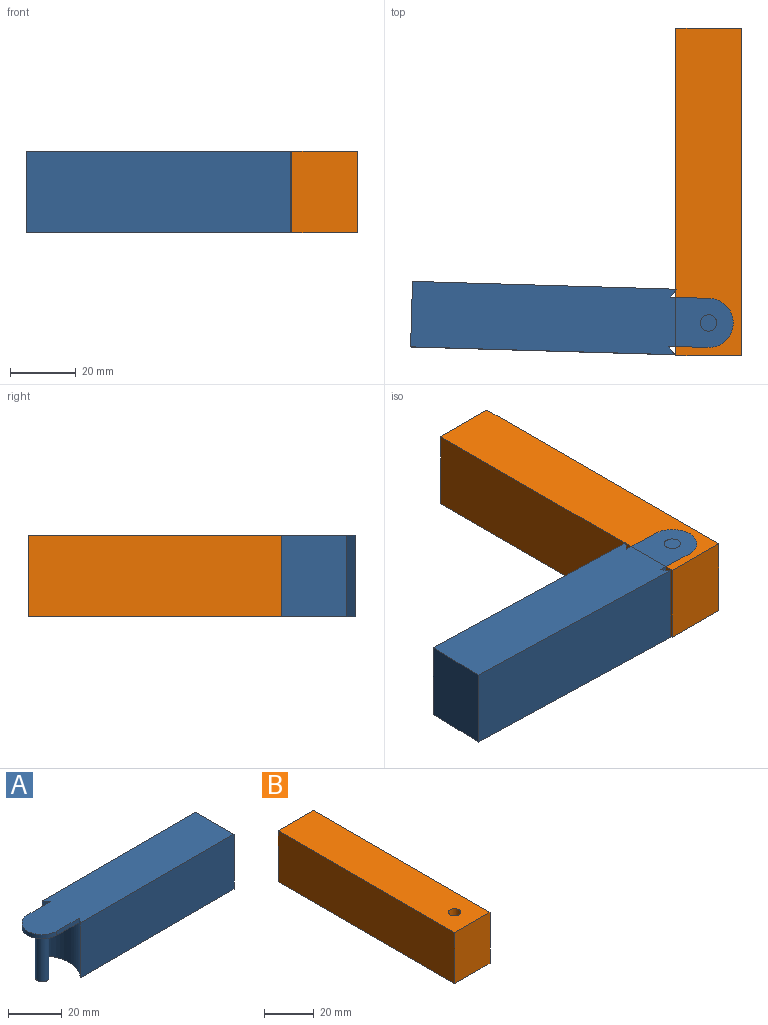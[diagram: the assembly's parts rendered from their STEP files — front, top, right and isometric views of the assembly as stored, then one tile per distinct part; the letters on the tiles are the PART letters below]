
ASSEMBLY  parts=2 mates=1
PART A: 12 faces, bbox 98.3x20x25 mm
  f0: cylinder r=14.14mm len=25mm, axis (0,0,-1), area 523.7mm2, adj f1,f3,f4,f5,f6,f8,f9
  f1: plane 80.76x25mm, normal (0,-1,0), area 2019.1mm2, adj f0,f2,f4,f5
  f2: plane 25x20mm, normal (1,0,0), area 500mm2, adj f1,f3,f4,f5
  f3: plane 80.76x25mm, normal (0,1,0), area 2019.1mm2, adj f0,f2,f4,f5
  f4: plane 98.26x20mm, normal (0,0,1), area 1848.3mm2, adj f0,f1,f2,f3,f7,f8,f9
  f5: plane 80.76x20mm, normal (0,0,-1), area 1558.2mm2, adj f0,f1,f2,f3
  f6: plane 21.64x15mm, normal (0,0,-1), area 270.4mm2, adj f0,f7,f8,f9,f10
  f7: cylinder r=7.5mm len=15mm, axis (0,0,1), area 47.1mm2, adj f4,f6,f8,f9
  f8: plane 11.99x2mm, normal (0,-1,0), area 24mm2, adj f0,f4,f6,f7
  f9: plane 11.99x2mm, normal (0,1,0), area 24mm2, adj f0,f4,f6,f7
  f10: cylinder r=2.5mm len=23mm, axis (0,0,1), area 361.3mm2, adj f6,f11
  f11: plane 5x5mm, normal (0,0,-1), area 19.6mm2, adj f10
PART B: 7 faces, bbox 20x100x25 mm
  f0: plane 100x25mm, normal (1,0,0), area 2500mm2, adj f1,f3,f4,f5
  f1: plane 25x20mm, normal (0,1,0), area 500mm2, adj f0,f2,f4,f5
  f2: plane 100x25mm, normal (-1,0,0), area 2500mm2, adj f1,f3,f4,f5
  f3: plane 25x20mm, normal (0,-1,0), area 500mm2, adj f0,f2,f4,f5
  f4: plane 100x20mm, normal (0,0,1), area 1980.4mm2, adj f0,f1,f2,f3,f6
  f5: plane 100x20mm, normal (0,0,-1), area 1980.4mm2, adj f0,f1,f2,f3,f6
  f6: cylinder r=2.5mm len=25mm, axis (0,0,1), area 392.7mm2, adj f4,f5
PLACE A rot(axis=(0,0,1),178.3deg) t=(-85.04,-25.63,0)mm
PLACE B at identity fixed
MATE revolute B.f6 <-> A.f0  axis (0,0,1) through (-42.33,-13.45,25)mm
